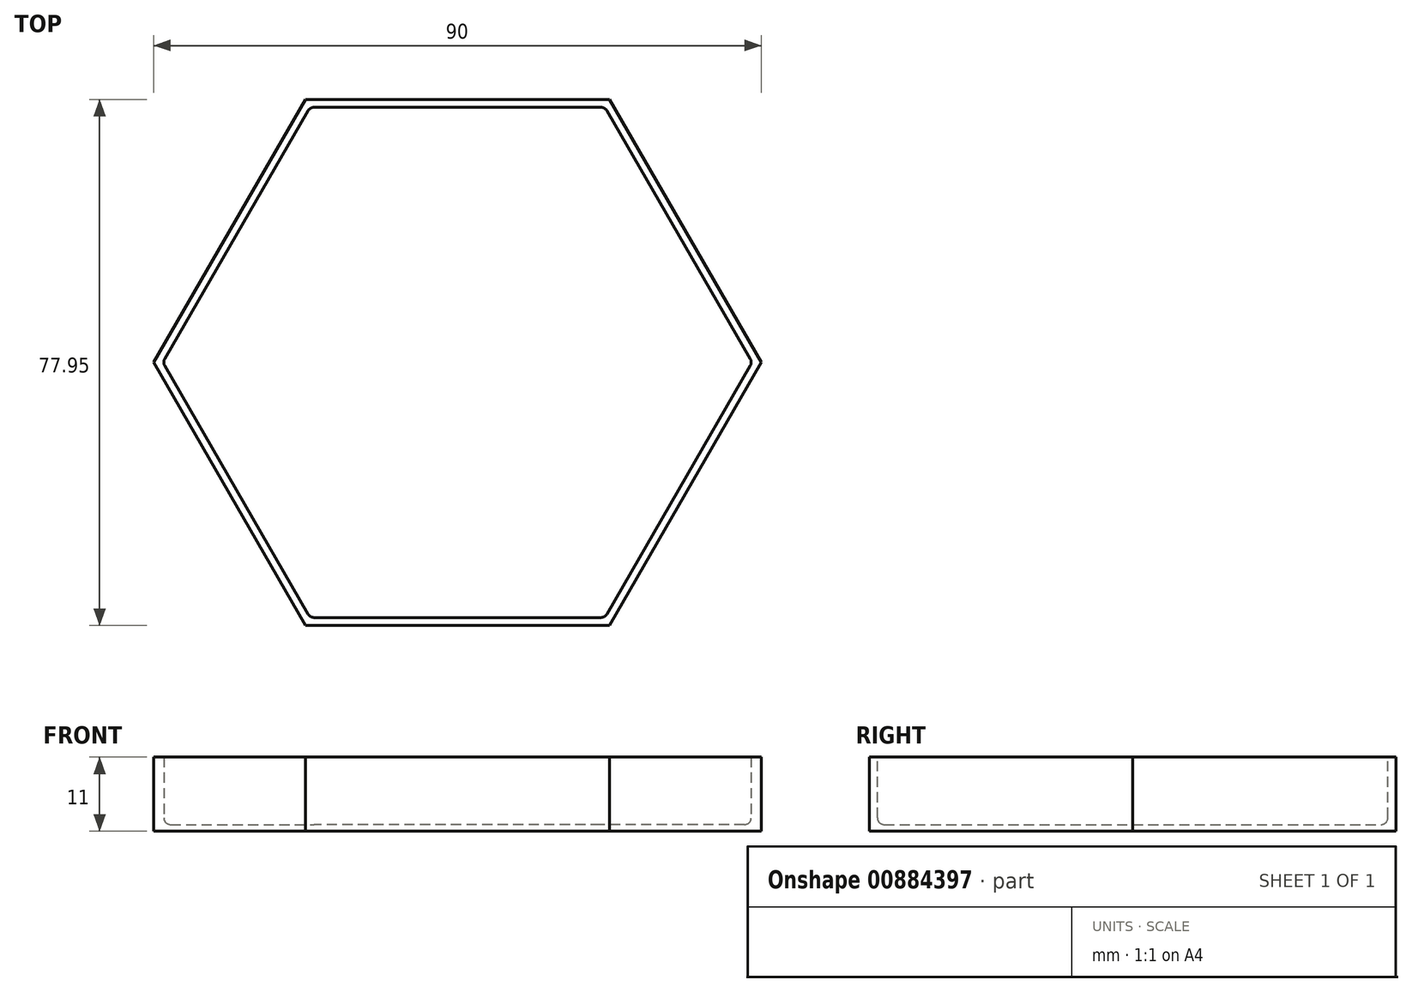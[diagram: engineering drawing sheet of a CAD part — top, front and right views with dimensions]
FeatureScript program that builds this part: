
annotation { "Feature Type Name" : "Feature", "Feature Type Description" : "" }
export const myFeature = defineFeature(function(context is Context, id is Id, definition is map)
    precondition{}
    {
        {
            var Q0;
            Q0=qCreatedBy(makeId("Top.planeOp"),FACE);
            var sketch = newSketch(context, id + "F0", { "sketchPlane" : qUnion([Q0])});
            skCircle(sketch, "E0.cCircle", {"center": v(-9.16, 11.6) * mm, "radius": 45 * mm, "construction": true});
            skLineSegment(sketch, "E0.0", {"start": v(35.84, 11.6) * mm, "end": v(13.35, -27.36) * mm});
            skLineSegment(sketch, "E0.1", {"start": v(13.35, -27.36) * mm, "end": v(-31.65, -27.37) * mm});
            skLineSegment(sketch, "E0.2", {"start": v(-31.65, -27.37) * mm, "end": v(-54.16, 11.6) * mm});
            skLineSegment(sketch, "E0.3", {"start": v(-54.16, 11.6) * mm, "end": v(-31.66, 50.58) * mm});
            skLineSegment(sketch, "E0.4", {"start": v(-31.66, 50.58) * mm, "end": v(13.34, 50.58) * mm});
            skLineSegment(sketch, "E0.5", {"start": v(13.34, 50.58) * mm, "end": v(35.84, 11.6) * mm});
            skSolve(sketch);
        }
        {
            var Q0;
            Q0=makeQuery(id+"F0.imprint","IMPRINT",FACE,{"disambiguationData":[TD([[makeQuery(id+"F0.imprint","IMPRINT",EDGE,{"derivedFrom":sQuery(id+"F0.wireOp",EDGE,"E0.0")}),-1.0]])]});
            extrude(context, id + "F1", {"entities" : qUnion([Q0]), "flatOperationType" : FlatOperationType.REMOVE, "depth" : 11 * mm, "offsetDistance" : 25.4 * mm, "domain" : OperationDomain.MODEL});
        }
        {
            var Q0;
            Q0=makeQuery(id+"F1.opExtrude","CAP_FACE",FACE,{"disambiguationData":[OSD([sQuery(id+"F0.wireOp",EDGE,"E0.0"),sQuery(id+"F0.wireOp",EDGE,"E0.1"),sQuery(id+"F0.wireOp",EDGE,"E0.2"),sQuery(id+"F0.wireOp",EDGE,"E0.3"),sQuery(id+"F0.wireOp",EDGE,"E0.4"),sQuery(id+"F0.wireOp",EDGE,"E0.5")])],"isStart":false});
            var sketch = newSketch(context, id + "F2", { "sketchPlane" : qUnion([Q0])});
            skCircle(sketch, "E1.cCircle", {"center": v(-9.16, 11.6) * mm, "radius": 37.8 * mm, "construction": true});
            skLineSegment(sketch, "E1.0", {"start": v(-30.98, 49.4) * mm, "end": v(12.67, 49.4) * mm});
            skLineSegment(sketch, "E1.1", {"start": v(12.67, 49.4) * mm, "end": v(34.5, 11.6) * mm});
            skLineSegment(sketch, "E1.2", {"start": v(34.5, 11.6) * mm, "end": v(12.67, -26.2) * mm});
            skLineSegment(sketch, "E1.3", {"start": v(12.67, -26.2) * mm, "end": v(-30.98, -26.2) * mm});
            skLineSegment(sketch, "E1.4", {"start": v(-30.98, -26.2) * mm, "end": v(-52.8, 11.6) * mm});
            skLineSegment(sketch, "E1.5", {"start": v(-52.8, 11.6) * mm, "end": v(-30.98, 49.4) * mm});
            skPoint(sketch, "E1.0.midPoint", {"position": v(-9.16, 49.4) * mm});
            skSolve(sketch);
        }
        {
            var Q0;
            Q0=makeQuery(id+"F2.imprint","IMPRINT",FACE,{"disambiguationData":[TD([[makeQuery(id+"F2.imprint","IMPRINT",EDGE,{"derivedFrom":sQuery(id+"F2.wireOp",EDGE,"E1.0")}),-1.0]])]});
            extrude(context, id + "F3", {"entities" : qUnion([Q0]), "operationType" : NewBodyOperationType.REMOVE, "flatOperationType" : FlatOperationType.REMOVE, "oppositeDirection" : true, "depth" : 10 * mm, "offsetDistance" : 25 * mm, "domain" : OperationDomain.MODEL});
        }
        {
            var Q0;
            Q0=makeQuery(id+"F3.boolean.opBoolean","COPY",EDGE,{"derivedFrom":makeQuery(id+"F3.opExtrude","CAP_EDGE",EDGE,{"disambiguationData":[OSD([sQuery(id+"F2.wireOp",EDGE,"E1.0")])],"isStart":false})});
            var Q1;
            Q1=makeQuery(id+"F3.boolean.opBoolean","COPY",EDGE,{"derivedFrom":makeQuery(id+"F3.opExtrude","CAP_EDGE",EDGE,{"disambiguationData":[OSD([sQuery(id+"F2.wireOp",EDGE,"E1.5")])],"isStart":false})});
            var Q2;
            Q2=makeQuery(id+"F3.boolean.opBoolean","COPY",EDGE,{"derivedFrom":makeQuery(id+"F3.opExtrude","CAP_EDGE",EDGE,{"disambiguationData":[OSD([sQuery(id+"F2.wireOp",EDGE,"E1.1")])],"isStart":false})});
            var Q3;
            Q3=makeQuery(id+"F3.boolean.opBoolean","COPY",EDGE,{"derivedFrom":makeQuery(id+"F3.opExtrude","CAP_EDGE",EDGE,{"disambiguationData":[OSD([sQuery(id+"F2.wireOp",EDGE,"E1.2")])],"isStart":false})});
            var Q4;
            Q4=makeQuery(id+"F3.boolean.opBoolean","COPY",EDGE,{"derivedFrom":makeQuery(id+"F3.opExtrude","CAP_EDGE",EDGE,{"disambiguationData":[OSD([sQuery(id+"F2.wireOp",EDGE,"E1.3")])],"isStart":false})});
            var Q5;
            Q5=makeQuery(id+"F3.boolean.opBoolean","COPY",EDGE,{"derivedFrom":makeQuery(id+"F3.opExtrude","CAP_EDGE",EDGE,{"disambiguationData":[OSD([sQuery(id+"F2.wireOp",EDGE,"E1.4")])],"isStart":false})});
            var Q6;
            Q6=makeQuery(id+"F3.boolean.opBoolean","COPY",EDGE,{"derivedFrom":makeQuery(id+"F3.opExtrude","SWEPT_EDGE",EDGE,{"disambiguationData":[OSD([sQuery(id+"F2.wireOp",EDGE,"E1.0"),sQuery(id+"F2.wireOp",EDGE,"E1.5")])]})});
            var Q7;
            Q7=makeQuery(id+"F3.boolean.opBoolean","COPY",EDGE,{"derivedFrom":makeQuery(id+"F3.opExtrude","SWEPT_EDGE",EDGE,{"disambiguationData":[OSD([sQuery(id+"F2.wireOp",EDGE,"E1.0"),sQuery(id+"F2.wireOp",EDGE,"E1.1")])]})});
            var Q8;
            Q8=makeQuery(id+"F3.boolean.opBoolean","COPY",EDGE,{"derivedFrom":makeQuery(id+"F3.opExtrude","SWEPT_EDGE",EDGE,{"disambiguationData":[OSD([sQuery(id+"F2.wireOp",EDGE,"E1.1"),sQuery(id+"F2.wireOp",EDGE,"E1.2")])]})});
            var Q9;
            Q9=makeQuery(id+"F3.boolean.opBoolean","COPY",EDGE,{"derivedFrom":makeQuery(id+"F3.opExtrude","SWEPT_EDGE",EDGE,{"disambiguationData":[OSD([sQuery(id+"F2.wireOp",EDGE,"E1.2"),sQuery(id+"F2.wireOp",EDGE,"E1.3")])]})});
            var Q10;
            Q10=makeQuery(id+"F3.boolean.opBoolean","COPY",EDGE,{"derivedFrom":makeQuery(id+"F3.opExtrude","SWEPT_EDGE",EDGE,{"disambiguationData":[OSD([sQuery(id+"F2.wireOp",EDGE,"E1.4"),sQuery(id+"F2.wireOp",EDGE,"E1.5")])]})});
            var Q11;
            Q11=makeQuery(id+"F3.boolean.opBoolean","COPY",EDGE,{"derivedFrom":makeQuery(id+"F3.opExtrude","SWEPT_EDGE",EDGE,{"disambiguationData":[OSD([sQuery(id+"F2.wireOp",EDGE,"E1.3"),sQuery(id+"F2.wireOp",EDGE,"E1.4")])]})});
            fillet(context, id + "F4", {"entities" : qUnion([Q0, Q1, Q2, Q3, Q4, Q5, Q6, Q7, Q8, Q9, Q10, Q11]), "radius" : 1 * mm, "tangentPropagation" : true, "allowEdgeOverflow" : false});
        }
    });
